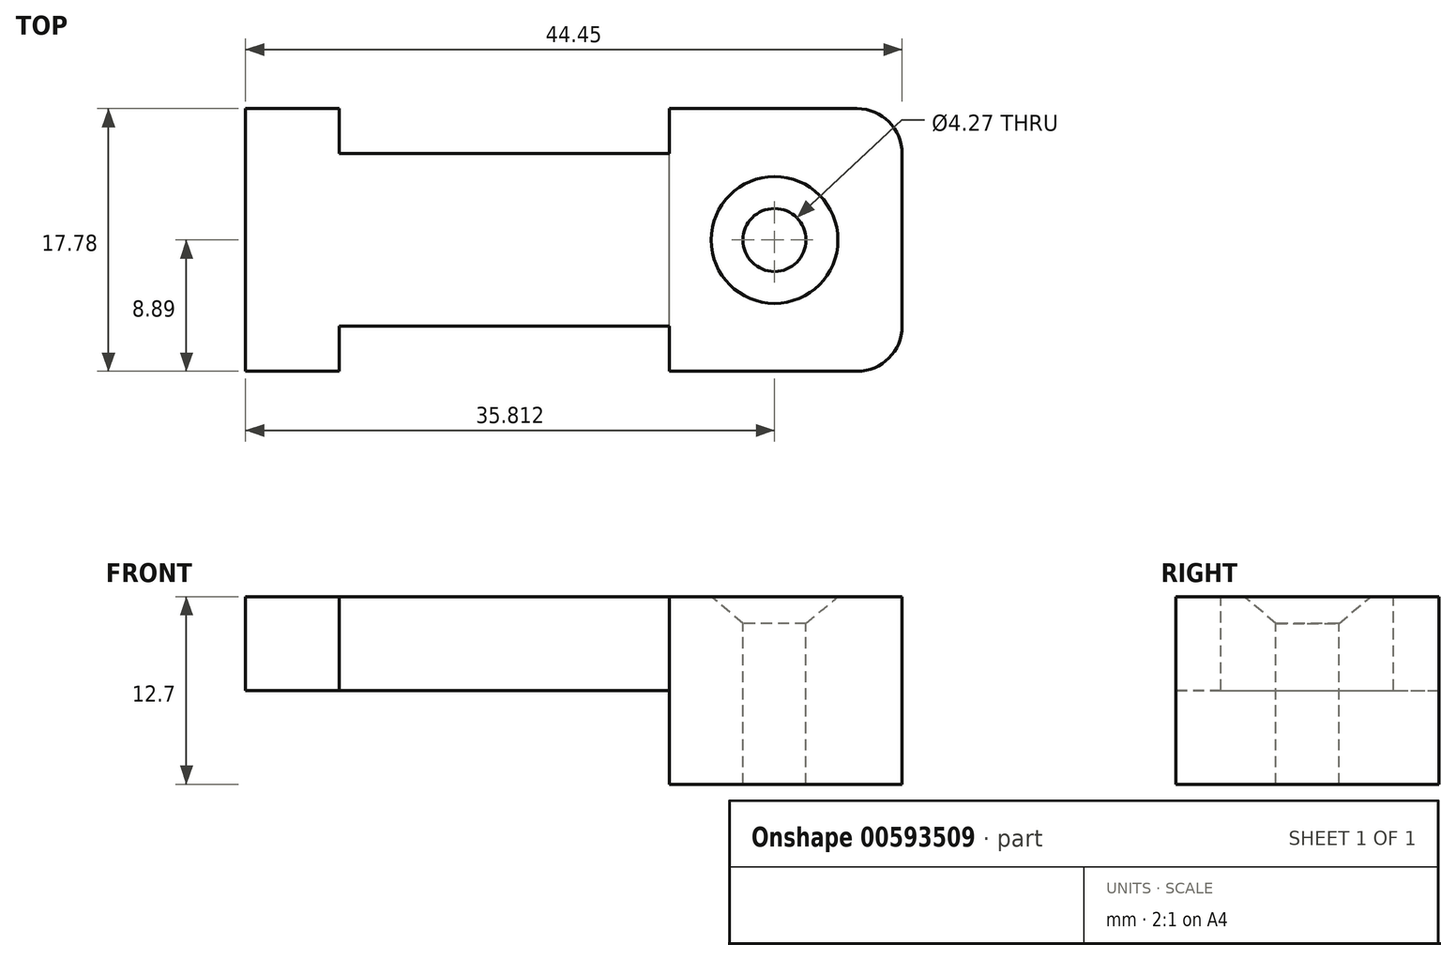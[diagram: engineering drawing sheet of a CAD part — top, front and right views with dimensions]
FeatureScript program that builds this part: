
annotation { "Feature Type Name" : "Feature", "Feature Type Description" : "" }
export const myFeature = defineFeature(function(context is Context, id is Id, definition is map)
    precondition{}
    {
        {
            var Q0;
            Q0=qCreatedBy(makeId("Front.planeOp"),FACE);
            var sketch = newSketch(context, id + "F0", { "sketchPlane" : qUnion([Q0])});
            skLineSegment(sketch, "E0", {"start": v(15.75, 0) * mm, "end": v(-28.7, 0) * mm});
            skLineSegment(sketch, "E1", {"start": v(-28.7, 0) * mm, "end": v(-28.7, -6.35) * mm});
            skLineSegment(sketch, "E2", {"start": v(-28.7, -6.35) * mm, "end": v(0, -6.35) * mm});
            skLineSegment(sketch, "E3", {"start": v(0, -6.35) * mm, "end": v(0, -12.7) * mm});
            skLineSegment(sketch, "E4", {"start": v(0, -12.7) * mm, "end": v(15.75, -12.7) * mm});
            skLineSegment(sketch, "E5", {"start": v(15.75, -12.7) * mm, "end": v(15.75, 0) * mm});
            skSolve(sketch);
        }
        {
            var Q0;
            Q0 = qSketchRegion(id + "F0", true);
            extrude(context, id + "F1", {"entities" : qUnion([Q0]), "depth" : 17.78 * mm, "offsetDistance" : 25.4 * mm});
        }
        {
            var Q0;
            Q0=makeQuery(id+"F1.opExtrude","SWEPT_FACE",FACE,{"disambiguationData":[OSD([sQuery(id+"F0.wireOp",EDGE,"E0")])]});
            var sketch = newSketch(context, id + "F2", { "sketchPlane" : qUnion([Q0])});
            skLineSegment(sketch, "E6.0", {"start": v(0, -14.73) * mm, "end": v(-22.35, -14.73) * mm});
            skLineSegment(sketch, "E7.0", {"start": v(0, -3.05) * mm, "end": v(-22.35, -3.05) * mm});
            skLineSegment(sketch, "E8", {"start": v(-22.35, -14.73) * mm, "end": v(-22.35, -22.45) * mm});
            skLineSegment(sketch, "E9", {"start": v(-22.35, -22.45) * mm, "end": v(0, -22.45) * mm});
            skLineSegment(sketch, "E10", {"start": v(0, -22.45) * mm, "end": v(0, -14.73) * mm});
            skLineSegment(sketch, "E11", {"start": v(-22.35, -3.05) * mm, "end": v(-22.35, 3.1) * mm});
            skLineSegment(sketch, "E12", {"start": v(-22.35, 3.1) * mm, "end": v(0, 3.1) * mm});
            skLineSegment(sketch, "E13", {"start": v(0, 3.1) * mm, "end": v(0, -3.05) * mm});
            skSolve(sketch);
        }
        {
            var Q0;
            Q0 = qSketchRegion(id + "F2", true);
            extrude(context, id + "F3", {"entities" : qUnion([Q0]), "operationType" : NewBodyOperationType.REMOVE, "endBound" : BoundingType.THROUGH_ALL, "oppositeDirection" : true, "depth" : 25.4 * mm, "offsetDistance" : 25.4 * mm});
        }
        {
            var Q0;
            Q0=makeQuery(id+"F1.opExtrude","CAP_EDGE",EDGE,{"disambiguationData":[OSD([sQuery(id+"F0.wireOp",EDGE,"E5")])],"isStart":true});
            var Q1;
            Q1=makeQuery(id+"F1.opExtrude","CAP_EDGE",EDGE,{"disambiguationData":[OSD([sQuery(id+"F0.wireOp",EDGE,"E5")])],"isStart":false});
            fillet(context, id + "F4", {"entities" : qUnion([Q0, Q1]), "radius" : 3.05 * mm, "tangentPropagation" : true, "allowEdgeOverflow" : false});
        }
        {
            var Q0;
            Q0=makeQuery(id+"F1.opExtrude","SWEPT_FACE",FACE,{"disambiguationData":[OSD([sQuery(id+"F0.wireOp",EDGE,"E0")])]});
            var sketch = newSketch(context, id + "F5", { "sketchPlane" : qUnion([Q0])});
            skPoint(sketch, "E14", {"position": v(7.11, -8.9) * mm});
            skSolve(sketch);
        }
        {
            var Q0;
            Q0=sQuery(id+"F5.wireOp",VERTEX,"E14");
            var Q1;
            Q1=makeQuery(id+"F1.opExtrude","SWEPT_BODY",BODY,{"disambiguationData":[OSD([sQuery(id+"F0.wireOp",EDGE,"E0"),sQuery(id+"F0.wireOp",EDGE,"E1"),sQuery(id+"F0.wireOp",EDGE,"E2"),sQuery(id+"F0.wireOp",EDGE,"E3"),sQuery(id+"F0.wireOp",EDGE,"E4"),sQuery(id+"F0.wireOp",EDGE,"E5")])]});
            hole(context, id + "F6", {"style" : HoleStyle.C_SINK, "endStyle" : HoleEndStyle.THROUGH, "holeDiameter" : 4.27 * mm, "cSinkDiameter" : 8.6 * mm, "cSinkAngle" : 100 * degree, "majorDiameter" : 6.35 * mm, "isTappedThrough" : true, "tappedDepth" : 12.7 * mm, "tapClearance" : 3, "startFromSketch" : true, "locations" : qUnion([Q0]), "scope" : qUnion([Q1])});
        }
    });
